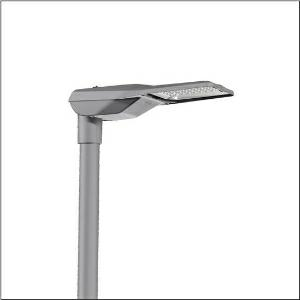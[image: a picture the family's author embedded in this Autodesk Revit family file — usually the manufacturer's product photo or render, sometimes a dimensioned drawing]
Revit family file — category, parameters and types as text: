
# Revit family: streetlight_sl_21_mini___stw1_0a_5xe2e43s08gb_9e9f
name_source: partatom
category: Lighting Fixtures
units: mm (PartAtom-declared; Revit-internal decimal feet)

## family parameters
Cut with Voids When Loaded = No
Host = Face
Light Source = No
Part Type = Normal
Room Calculation Point = No
Round Connector Dimension = Use Diameter
Shared = No

## types (1)
- --- (1 x LED, 6180 lm, 40.4 W, 4000K)
    Apparent Load = 40 VA
    CIE Flux Codes = 38 75 98 100 100
    Color Rendering = 70
    Color Temperature = 4000K
    Default Elevation = 1800 mm
    Description = Streetlight SL 21 mini, mast luminaire, primary light control with lens, of PMMA, primary optical cover: cover, of toughened safety glass, transparent, light distribution: STW1.0a, light emission: direct distribution, primary light characteristic: asymmetric, installation type: side-entry, post-top, LED, High Power LED, rated luminous flux: 6.180lm, luminous efficacy: 153lm/W, light colour: 740, colour temperature: 4000K, control gear: D4i, control: overheat protection, constant luminous flux control, time-dependent luminous flux control, flexible luminous flux parameterisation, pre-setting: logarithmic dimming characteristic, mains connection: 220..240V, AC, 50/60Hz, start of lifetime: 40W, end of service life: 41W, reduction: 19W, luminaire housing, of diecast aluminium, powder-coated, Siteco® metallic grey (DB 702S), corrosivity category C5 mid according to DIN EN ISO 12944, please order mast flange separately, inclination adjustable: 0°, 5°, 10°, 15°, sealing non-destructively replaceable, multi-level sealing system, length: 628mm, width: 235mm, height: 110mm, mast flange for spigot size: 42mm (side-entry): 5XC10008XM4, 60/48mm (side-entry/post-top): 5XC10108XM2, 76/60mm (side-entry/post-top): 5XC10108XM1, mounting height: 4..8m, Smart Interface above, protection rating (complete): IP66, insulation class (complete): insulation class II (safety insulation), certification: CE, ENEC, ENEC+, VDE, impact resistance: IK10, permissible operating ambient temperature for outdoor applications: -40..+50°C, standard-compliant lighting for roads and squares, packaging unit: 1 piece

Light Distribution: STW1.0a
    Height = 110 mm
    Lamp = 1 x LED
    Lamp Light Flux = 6180 lm
    Lamp Power = 40.4 W
    Lamp count = 1
    Length = 625 mm
    Luminous efficacy = 153 lm/W
    Manufacturer = Siteco
    ModVariant = No
    Model = 5XE2E43S08GB
    Number of Poles = 1
    OnlyDefault = Yes
    Power Factor = 1
    Product Name = Streetlight SL 21 mini | STW1.0a
    Product group = mast luminaire | pylon top
    ProductGroupID = 6100
    Protection Class = Protection class II
    Protection Degree = IP 66
    RLX_Detail_Level = 1
    RLX_Emergency_Light_Flux = 0 lm
    RLX_Emergency_Type = 0
    RLX_Emergency_Type_DB = No
    RlxData = <blob elided: 26201 chars, md5=3d0b0dd6>
    Socket = socket
    Standby Power = 0 W
    System Light Flux = 6180 lm
    System Power = 40 W
    Type Comments = factory setting: luminous flux: 100 % | dim-lin: 254 | 812 mA
    Type Image = l_1003515.jpg
    URL = http://relux.com
    VarID = @adj_187406
    Voltage = 0 V
    Weight = 0.00 kg
    Width = 234 mm

## geometry (parser evidence)
native form markers: Blend x4, Sweep x10
no freeform markers — native parametric forms only
